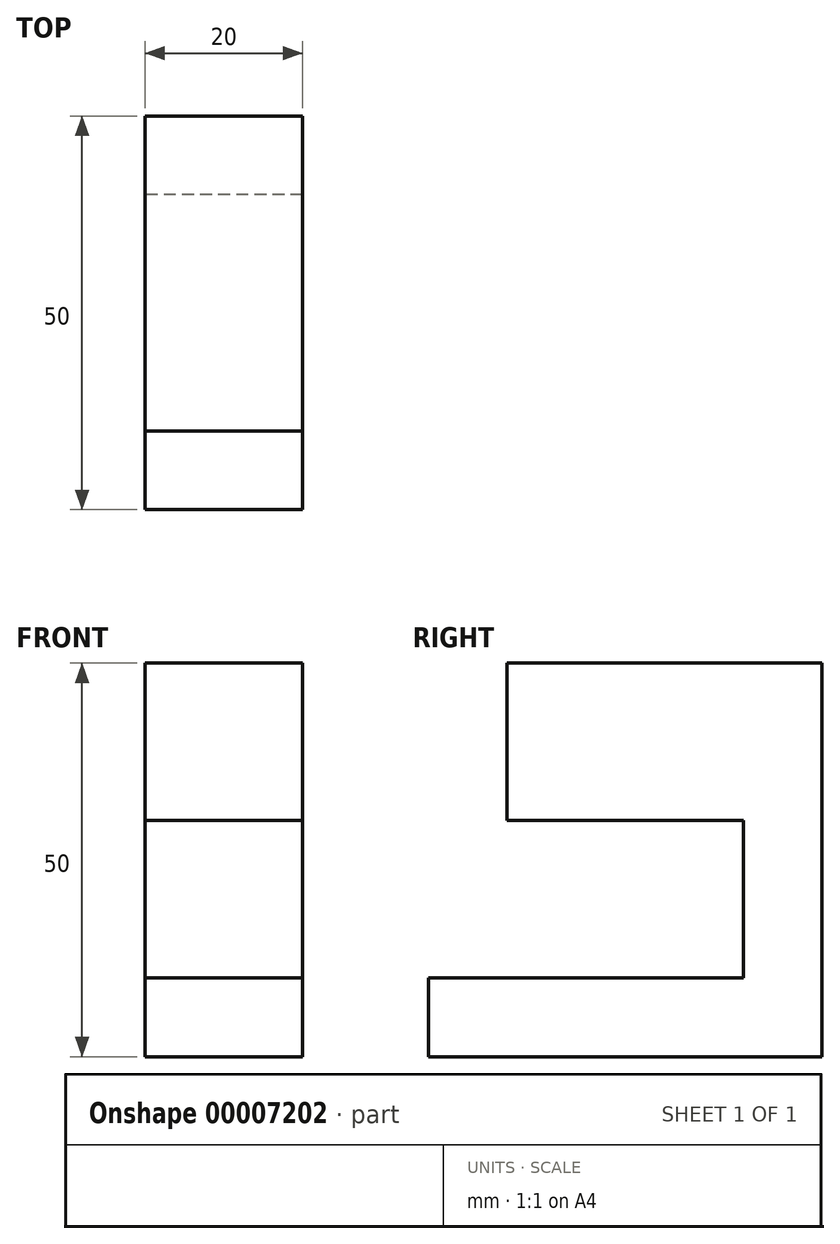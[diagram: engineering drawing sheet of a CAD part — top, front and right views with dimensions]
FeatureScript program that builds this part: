
annotation { "Feature Type Name" : "Feature", "Feature Type Description" : "" }
export const myFeature = defineFeature(function(context is Context, id is Id, definition is map)
    precondition{}
    {
        {
            var Q0;
            Q0=qCreatedBy(makeId("Right.planeOp"),FACE);
            var sketch = newSketch(context, id + "F0", { "sketchPlane" : qUnion([Q0])});
            skLineSegment(sketch, "E0.bottom", {"start": v(-12.22, 24.02) * mm, "end": v(27.78, 24.02) * mm});
            skLineSegment(sketch, "E0.top", {"start": v(-22.22, -25.98) * mm, "end": v(27.78, -25.98) * mm});
            skLineSegment(sketch, "E0.left", {"start": v(-12.22, 24.02) * mm, "end": v(-12.22, 4.02) * mm});
            skLineSegment(sketch, "E0.right", {"start": v(27.78, 24.02) * mm, "end": v(27.78, -25.98) * mm});
            skPoint(sketch, "E1", {"position": v(-12.22, 4.02) * mm});
            skPoint(sketch, "E2", {"position": v(-22.22, -15.98) * mm});
            skPoint(sketch, "E3", {"position": v(17.78, 4.02) * mm});
            skPoint(sketch, "E4", {"position": v(17.78, -15.98) * mm});
            skLineSegment(sketch, "E5", {"start": v(-12.22, 4.02) * mm, "end": v(17.78, 4.02) * mm});
            skLineSegment(sketch, "E6", {"start": v(17.78, 4.02) * mm, "end": v(17.78, -15.98) * mm});
            skLineSegment(sketch, "E7", {"start": v(17.78, -15.98) * mm, "end": v(-22.22, -15.98) * mm});
            skLineSegment(sketch, "E8.trimOffspring", {"start": v(-22.22, -15.98) * mm, "end": v(-22.22, -25.98) * mm});
            skSolve(sketch);
        }
        {
            var Q0;
            Q0 = qSketchRegion(id + "F0", true);
            extrude(context, id + "F1", {"entities" : qUnion([Q0]), "depth" : 20 * mm});
        }
    });
